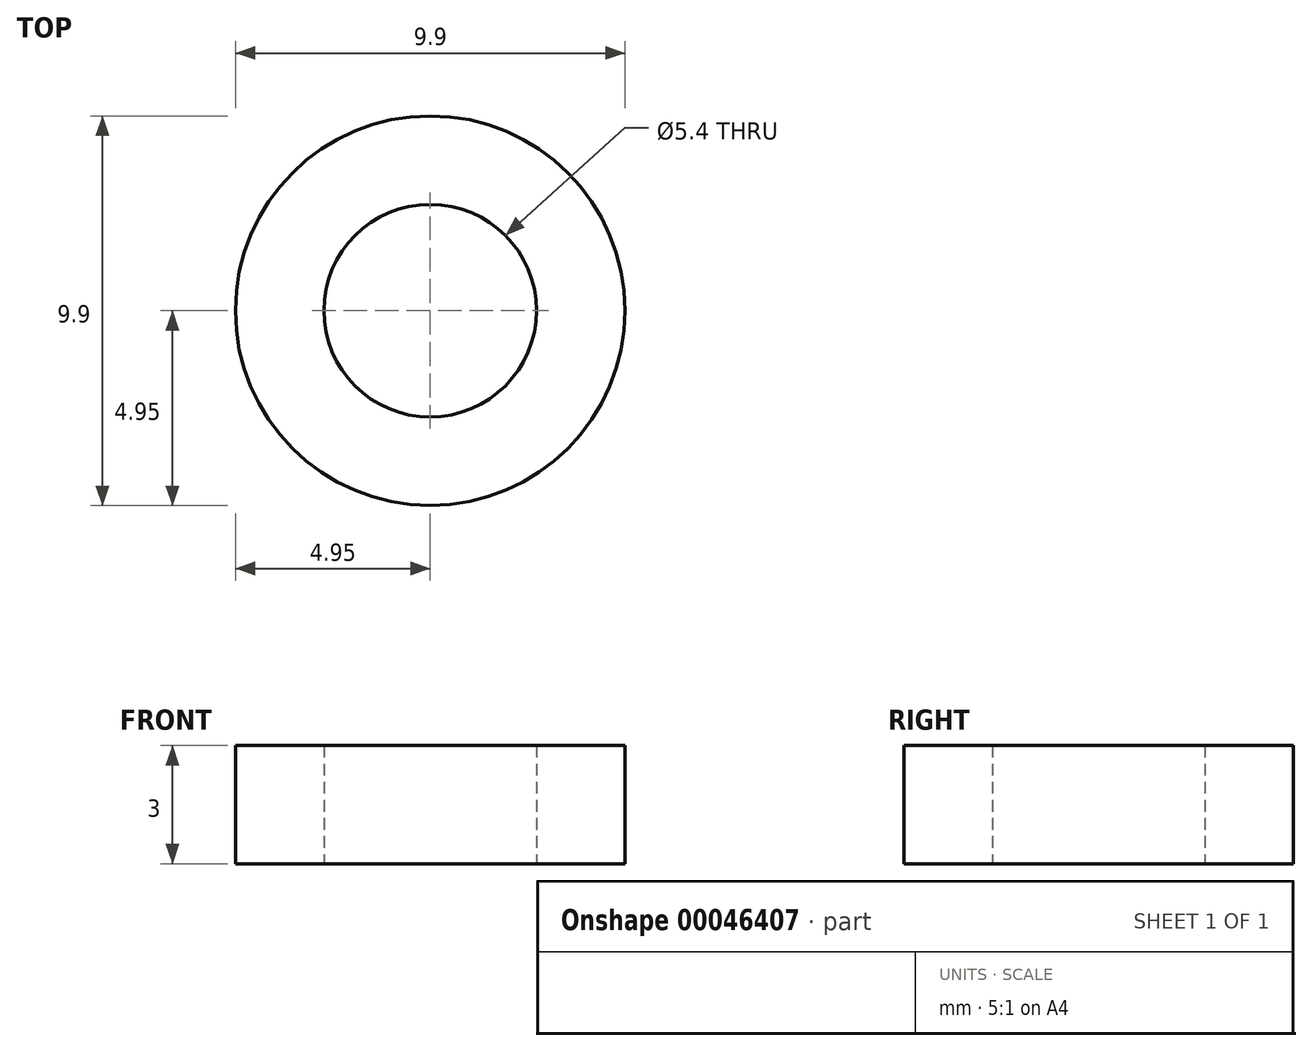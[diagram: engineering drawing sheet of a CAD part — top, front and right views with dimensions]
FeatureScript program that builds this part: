
annotation { "Feature Type Name" : "Feature", "Feature Type Description" : "" }
export const myFeature = defineFeature(function(context is Context, id is Id, definition is map)
    precondition{}
    {
        {
            var Q0;
            Q0=qCreatedBy(makeId("Top.planeOp"),FACE);
            var sketch = newSketch(context, id + "F0", { "sketchPlane" : qUnion([Q0])});
            skCircle(sketch, "E0", {"center": v(0, 0) * mm, "radius": 2.7 * mm});
            skCircle(sketch, "E1", {"center": v(0, 0) * mm, "radius": 4.95 * mm});
            skSolve(sketch);
        }
        {
            var Q0;
            Q0=makeQuery(id+"F0.imprint","IMPRINT",FACE,{"disambiguationData":[TD([[makeQuery(id+"F0.imprint","IMPRINT",EDGE,{"derivedFrom":sQuery(id+"F0.wireOp",EDGE,"E0")}),-1.0]])]});
            extrude(context, id + "F1", {"entities" : qUnion([Q0]), "depth" : 3 * mm, "offsetDistance" : 25 * mm});
        }
    });
